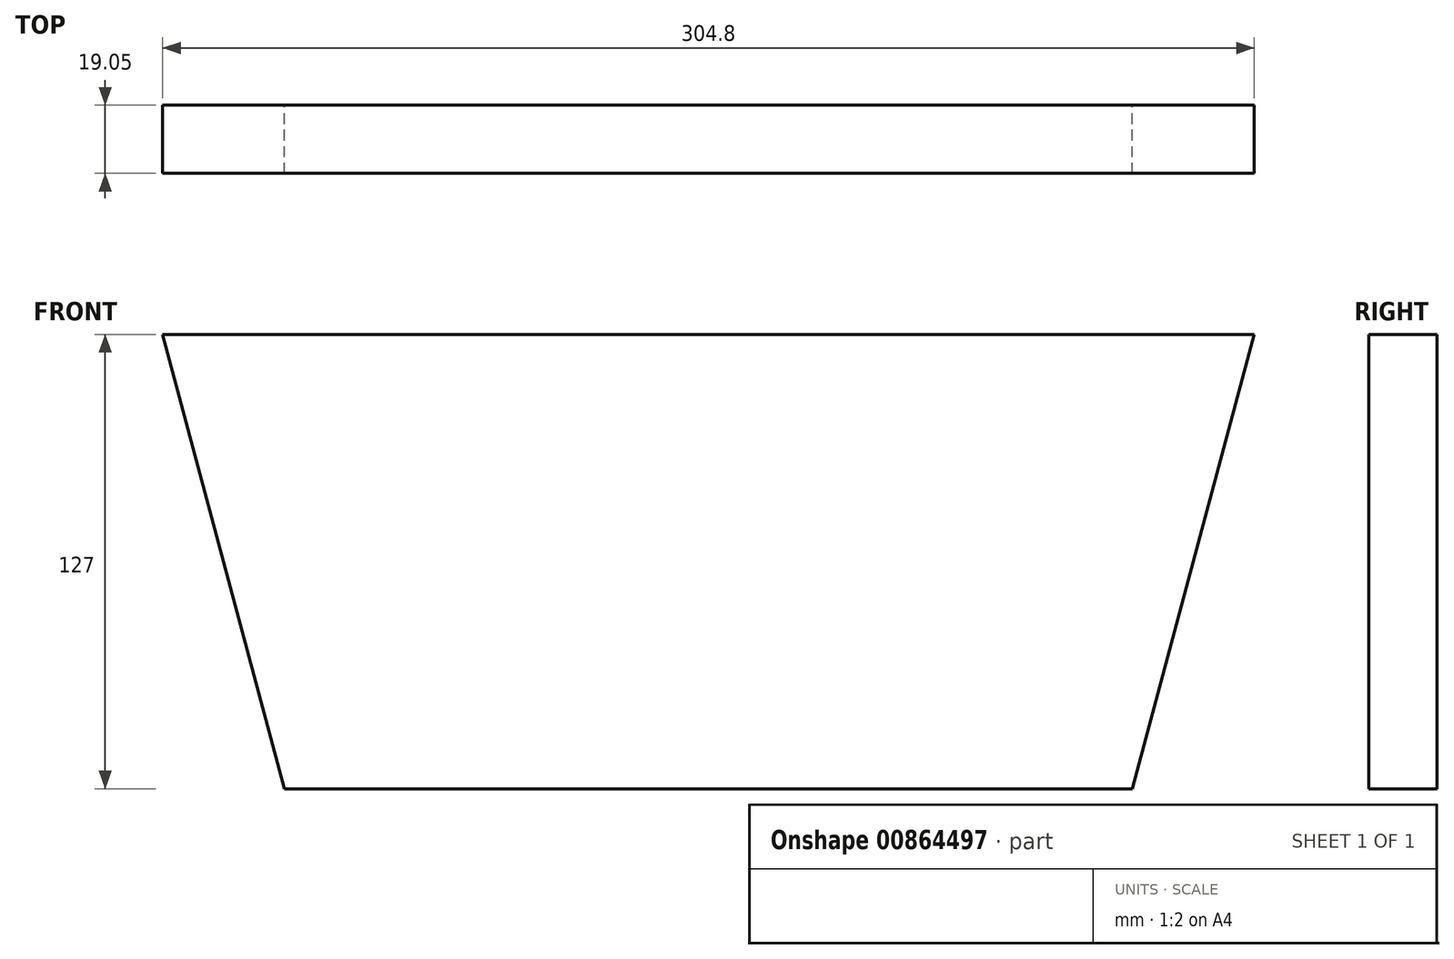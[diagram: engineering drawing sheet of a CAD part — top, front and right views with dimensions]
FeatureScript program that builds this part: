
annotation { "Feature Type Name" : "Feature", "Feature Type Description" : "" }
export const myFeature = defineFeature(function(context is Context, id is Id, definition is map)
    precondition{}
    {
        {
            var Q0;
            Q0=qCreatedBy(makeId("Front.planeOp"),FACE);
            var sketch = newSketch(context, id + "F0", { "sketchPlane" : qUnion([Q0])});
            skLineSegment(sketch, "E0.bottom", {"start": v(165.1, 63.5) * mm, "end": v(-139.7, 63.5) * mm});
            skLineSegment(sketch, "E0.top", {"start": v(131.07, -63.5) * mm, "end": v(-105.67, -63.5) * mm});
            skPoint(sketch, "E0.middle", {"position": v(0, 0) * mm});
            skLineSegment(sketch, "E1", {"start": v(-139.7, 63.5) * mm, "end": v(-105.67, -63.5) * mm});
            skLineSegment(sketch, "E2", {"start": v(165.1, 63.5) * mm, "end": v(131.07, -63.5) * mm});
            skPoint(sketch, "E3.orphan", {"position": v(-165.1, -63.5) * mm});
            skPoint(sketch, "E4.orphan", {"position": v(139.7, -63.5) * mm});
            skSolve(sketch);
        }
        {
            var Q0;
            Q0=makeQuery(id+"F0.imprint","IMPRINT",FACE,{"disambiguationData":[TD([[makeQuery(id+"F0.imprint","IMPRINT",EDGE,{"derivedFrom":sQuery(id+"F0.wireOp",EDGE,"E0.bottom")}),1.0]])]});
            extrude(context, id + "F1", {"entities" : qUnion([Q0]), "depth" : 19.05 * mm, "offsetDistance" : 25.4 * mm});
        }
    });
